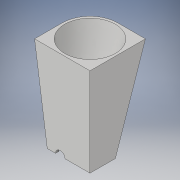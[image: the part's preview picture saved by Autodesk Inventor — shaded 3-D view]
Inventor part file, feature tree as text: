
AUTODESK INVENTOR PART (.ipt)
format: ipt  version: 2018 (Build 220112000, 112)  size: 161,280 bytes
history: native  units: in
note: dims shown in document units (in); Inventor stores cm internally (conversion verified against a paired STEP export)
features: sketch x5, loft x2, plane x1, extrude x1
ambient origin geometry x8: Origin, YZ Plane, XZ Plane, XY Plane, X Axis, Y Axis, Z Axis, Center Point
bodies: Solid1 (feature_tree)
feature tree (9):
  sketch  "Sketch1"  dims[d1=0.8in d2=1.35in]
  plane  "Work Plane1"
  loft  "Loft1"
  loft  "Loft2"
  extrude  "Extrusion1"  Depth=0.875in
  sketch  "Sketch3"  dims[d4=0.4in d5=2.8in]
  sketch  "Sketch4"  dims[d15=0.875in d17=0.875in]
  sketch  "Sketch5"  dims[d18=0.875in]
  sketch  "Sketch6"  dims[d19=0.0in d20=90.0deg d21=0.0in d22=90.0deg d23=1.6in d24=0.875in d26=0.875in d27=0.65in d28=0.0in d29=90.0deg d30=0.0in d31=90.0deg d32=0.4in d33=0.4in d34=0.4in d35=0.15in d36=0.0in d37=0.0in d38=3.0in d39=0.0in]
